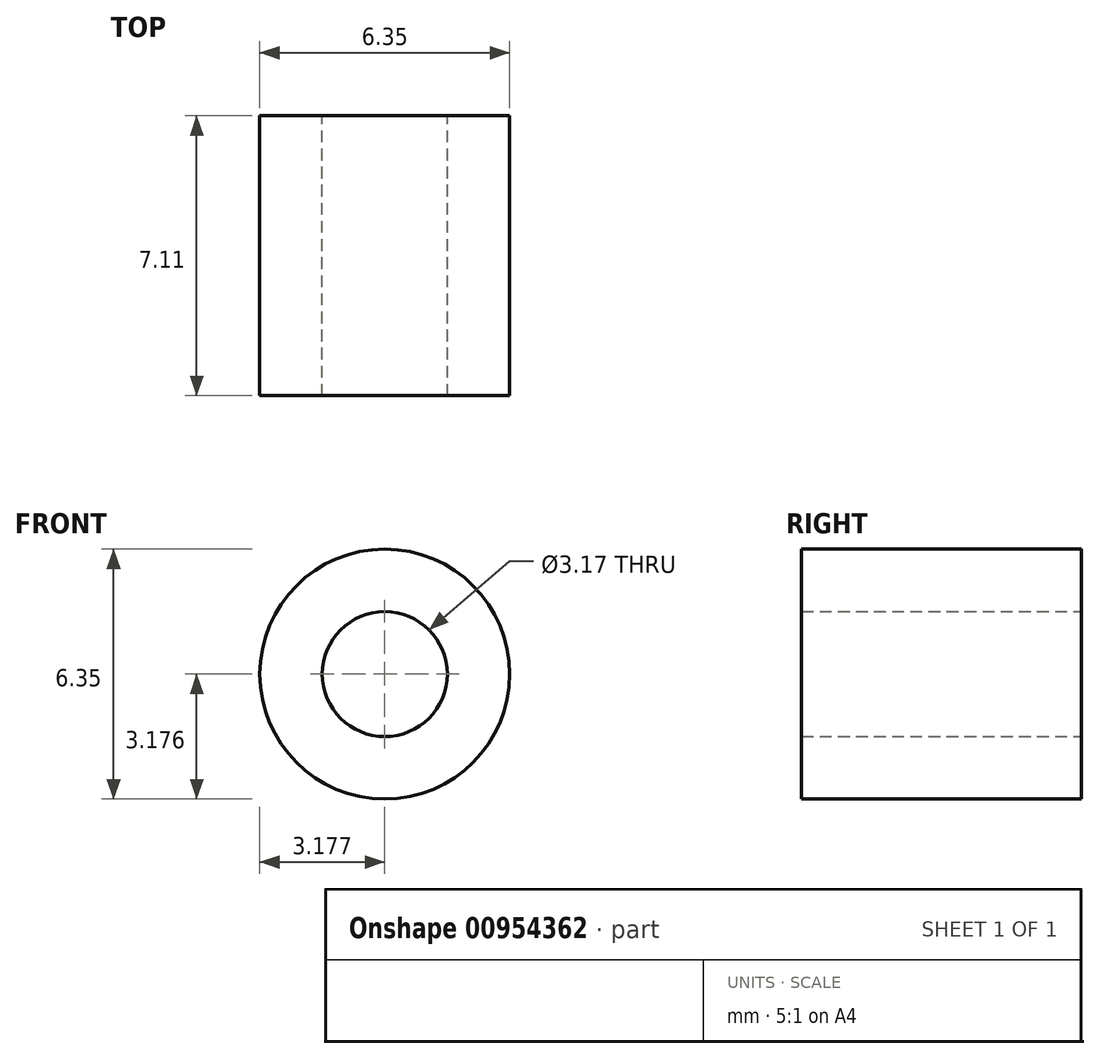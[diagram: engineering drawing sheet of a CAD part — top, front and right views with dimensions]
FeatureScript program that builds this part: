
annotation { "Feature Type Name" : "Feature", "Feature Type Description" : "" }
export const myFeature = defineFeature(function(context is Context, id is Id, definition is map)
    precondition{}
    {
        {
            var Q0;
            Q0=qCreatedBy(makeId("Front.planeOp"),FACE);
            var sketch = newSketch(context, id + "F0", { "sketchPlane" : qUnion([Q0])});
            skCircle(sketch, "E0", {"center": v(-48.78, 41.88) * mm, "radius": 3.18 * mm});
            skCircle(sketch, "E1", {"center": v(-48.78, 41.88) * mm, "radius": 1.59 * mm});
            skSolve(sketch);
        }
        {
            var Q0;
            Q0=makeQuery(id+"F0.imprint","IMPRINT",FACE,{"disambiguationData":[TD([[makeQuery(id+"F0.imprint","IMPRINT",EDGE,{"derivedFrom":sQuery(id+"F0.wireOp",EDGE,"E0")}),1.0]])]});
            extrude(context, id + "F1", {"entities" : qUnion([Q0]), "depth" : 7.11 * mm, "offsetDistance" : 25.4 * mm});
        }
    });
